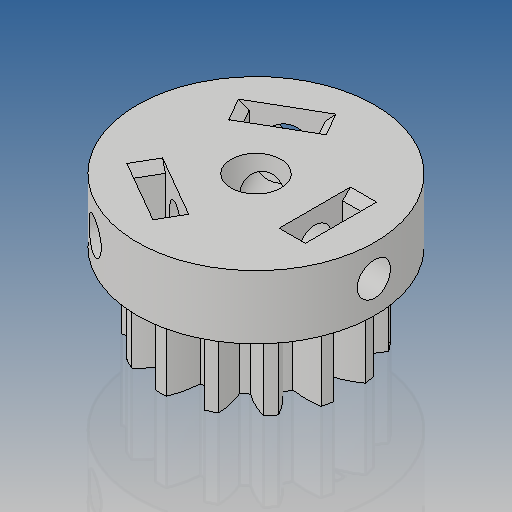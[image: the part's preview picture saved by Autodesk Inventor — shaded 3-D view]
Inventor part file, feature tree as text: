
AUTODESK INVENTOR PART (.ipt)
format: ipt  version: 2017 (Build 210142000, 142)  size: 308,736 bytes
history: native  units: mm
features: extrude x4, other x3, sketch x3, pattern_circular x1, chamfer x1, projected_geometry x1
ambient origin geometry x8: Origin, YZ Plane, XZ Plane, XY Plane, X Axis, Y Axis, Z Axis, Center Point
bodies: Body1 (feature_tree)
feature tree (13):
  other  "Sólido1"
  extrude  "Extrusión1"  Depth=11.85mm
  sketch  "Boceto2"  dims[d3=6.576542mm d4=3.3mm]
  extrude  "Extrusión2"  Depth=3.3mm
  extrude  "Extrusión3"  Depth=10.0mm
  extrude  "Extrusión4"  TaperAngle=120.0deg  [1 undecoded]
  other  "Dientes de engranaje recto3"
  pattern_circular  "Patrón circular1"  [2 undecoded]
  chamfer  "Chaflán1"  Distance=16.0mm
  sketch  "Boceto1"  dims[d0=6.3mm d2=11.85mm]
  projected_geometry  "Contorno proyectado1"
  sketch  "Boceto3"  dims[d5=8.0mm d6=0.0mm d7=4.2mm d8=120.0deg d9=3.7mm d10=16.0mm d11=0.0mm d12=4.0mm d13=0.0mm d14=10.0mm d15=0.0mm d16=30.0mm d18=360.0deg d20=30.0mm d21=360.0deg d23=1.0mm d24=2.0mm d25=45.0deg d26=30.0mm d27=4.275mm d28=4.275mm]
  other  "iFeature1:3"
note: 3 required parameter values undecoded (feature->parameter linkage not recoverable at this tier; creation-order binding heuristic only, values carry confidence <= 0.55)
